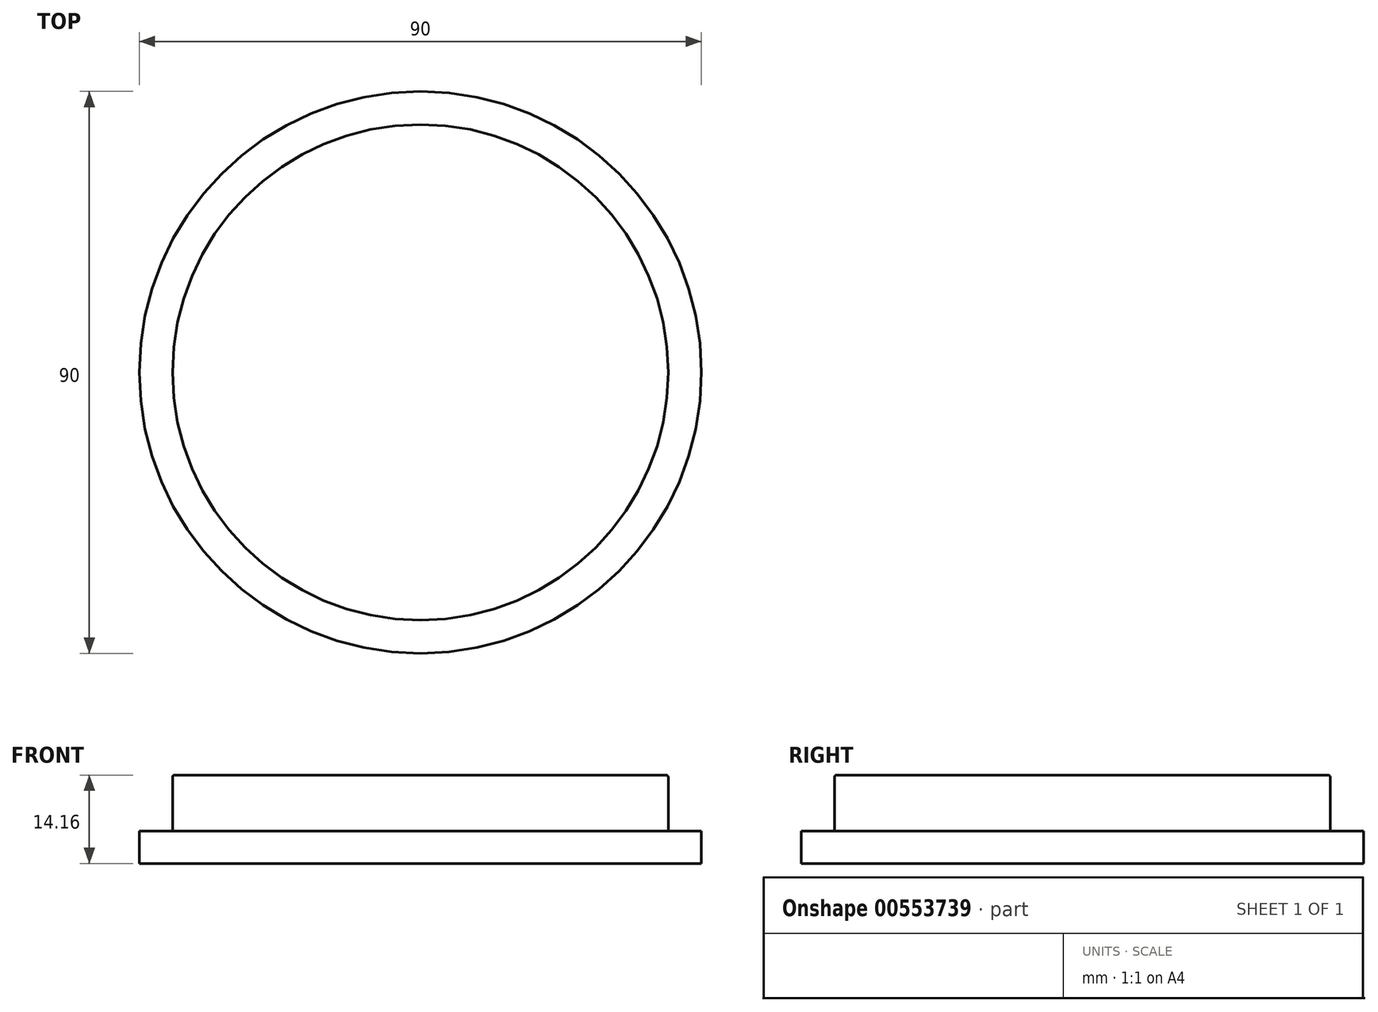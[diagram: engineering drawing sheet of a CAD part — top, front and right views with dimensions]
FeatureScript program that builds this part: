
annotation { "Feature Type Name" : "Feature", "Feature Type Description" : "" }
export const myFeature = defineFeature(function(context is Context, id is Id, definition is map)
    precondition{}
    {
        {
            var Q0;
            Q0=qCreatedBy(makeId("Front.planeOp"),FACE);
            var sketch = newSketch(context, id + "F0", { "sketchPlane" : qUnion([Q0])});
            skLineSegment(sketch, "E0", {"start": v(0, 60) * mm, "end": v(0, -60) * mm});
            skLineSegment(sketch, "E1", {"start": v(-70, 0) * mm, "end": v(70, 0) * mm});
            skLineSegment(sketch, "E2", {"start": v(-39.7, 5.16) * mm, "end": v(-39.7, 13.8) * mm});
            skLineSegment(sketch, "E3", {"start": v(-39.34, 14.16) * mm, "end": v(0, 14.16) * mm});
            skLineSegment(sketch, "E4", {"start": v(-39.7, 5.16) * mm, "end": v(-45, 5.16) * mm});
            skLineSegment(sketch, "E5", {"start": v(-45, 5.16) * mm, "end": v(-45, 0) * mm});
            skLineSegment(sketch, "E6", {"start": v(-45, 0) * mm, "end": v(0, 0) * mm});
            skLineSegment(sketch, "E7", {"start": v(0, 14.16) * mm, "end": v(0, 0) * mm});
            skArc(sketch, "E8", {"start": v(-39.34, 14.16) * mm, "mid": v(-39.59, 14.06) * mm, "end": v(-39.7, 13.8) * mm});
            skSolve(sketch);
        }
        {
            var Q0;
            Q0=makeQuery(id+"F0.imprint","IMPRINT",FACE,{"disambiguationData":[TD([[makeQuery(id+"F0.imprint","IMPRINT",EDGE,{"derivedFrom":sQuery(id+"F0.wireOp",EDGE,"E2")}),-1.0]])]});
            var Q1;
            Q1=sQuery(id+"F0.wireOp",EDGE,"E0");
            revolve(context, id + "F1", {"entities" : qUnion([Q0]), "axis" : qUnion([Q1]), "revolveType" : RevolveType.FULL});
        }
    });
